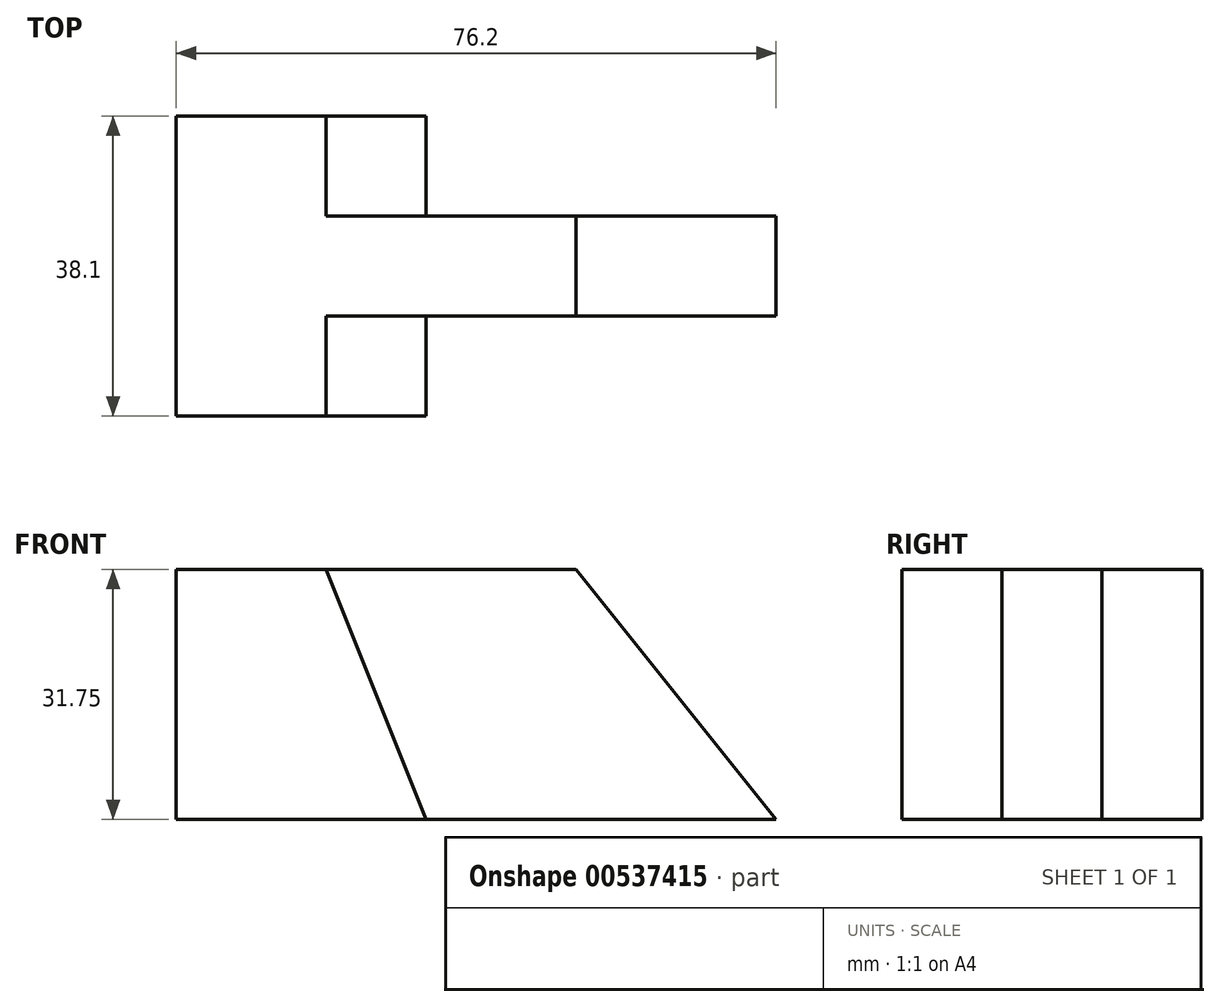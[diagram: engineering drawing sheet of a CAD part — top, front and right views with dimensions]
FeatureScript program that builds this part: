
annotation { "Feature Type Name" : "Feature", "Feature Type Description" : "" }
export const myFeature = defineFeature(function(context is Context, id is Id, definition is map)
    precondition{}
    {
        {
            var Q0;
            Q0=qCreatedBy(makeId("Front.planeOp"),FACE);
            var sketch = newSketch(context, id + "F0", { "sketchPlane" : qUnion([Q0])});
            skLineSegment(sketch, "E0", {"start": v(0, 31.75) * mm, "end": v(0, 0) * mm});
            skLineSegment(sketch, "E1", {"start": v(0, 0) * mm, "end": v(76.2, 0) * mm});
            skLineSegment(sketch, "E2", {"start": v(76.2, 0) * mm, "end": v(76.2, 31.75) * mm});
            skLineSegment(sketch, "E3", {"start": v(76.2, 31.75) * mm, "end": v(0, 31.75) * mm});
            skSolve(sketch);
        }
        {
            var Q0;
            Q0=makeQuery(id+"F0.imprint","IMPRINT",FACE,{"disambiguationData":[TD([[makeQuery(id+"F0.imprint","IMPRINT",EDGE,{"derivedFrom":sQuery(id+"F0.wireOp",EDGE,"E0")}),1.0]])]});
            extrude(context, id + "F1", {"entities" : qUnion([Q0]), "depth" : 38.1 * mm, "offsetDistance" : 25.4 * mm});
        }
        {
            var Q0;
            Q0=makeQuery(id+"F1.opExtrude","SWEPT_FACE",FACE,{"disambiguationData":[OSD([sQuery(id+"F0.wireOp",EDGE,"E2")])]});
            var sketch = newSketch(context, id + "F2", { "sketchPlane" : qUnion([Q0])});
            skSolve(sketch);
        }
        {
            var Q0;
            Q0=makeQuery(id+"F1.opExtrude","CAP_FACE",FACE,{"disambiguationData":[OSD([sQuery(id+"F0.wireOp",EDGE,"E0"),sQuery(id+"F0.wireOp",EDGE,"E1"),sQuery(id+"F0.wireOp",EDGE,"E2"),sQuery(id+"F0.wireOp",EDGE,"E3")])],"isStart":false});
            var sketch = newSketch(context, id + "F3", { "sketchPlane" : qUnion([Q0])});
            skLineSegment(sketch, "E4", {"start": v(19.05, 31.75) * mm, "end": v(31.75, 0) * mm});
            skSolve(sketch);
        }
        {
            var Q0;
            {var subQ0=sQuery(id+"F3.wireOp",EDGE,"E4");Q0=makeQuery(id+"F3.imprint","IMPRINT",FACE,{"disambiguationData":[TD([[makeQuery(id+"F3.imprint","IMPRINT",EDGE,{"derivedFrom":subQ0}),1.0]])]});}
            extrude(context, id + "F4", {"entities" : qUnion([Q0]), "operationType" : NewBodyOperationType.REMOVE, "oppositeDirection" : true, "depth" : 12.7 * mm, "offsetDistance" : 25.4 * mm});
        }
        {
            var Q0;
            Q0=makeQuery(id+"F1.opExtrude","CAP_FACE",FACE,{"disambiguationData":[OSD([sQuery(id+"F0.wireOp",EDGE,"E0"),sQuery(id+"F0.wireOp",EDGE,"E1"),sQuery(id+"F0.wireOp",EDGE,"E2"),sQuery(id+"F0.wireOp",EDGE,"E3")])],"isStart":true});
            var sketch = newSketch(context, id + "F5", { "sketchPlane" : qUnion([Q0])});
            skLineSegment(sketch, "E5", {"start": v(-19.05, 31.75) * mm, "end": v(-31.75, 0) * mm});
            skSolve(sketch);
        }
        {
            var Q0;
            {var subQ0=sQuery(id+"F5.wireOp",EDGE,"E5");Q0=makeQuery(id+"F5.imprint","IMPRINT",FACE,{"disambiguationData":[TD([[makeQuery(id+"F5.imprint","IMPRINT",EDGE,{"derivedFrom":subQ0}),-1.0]])]});}
            extrude(context, id + "F6", {"entities" : qUnion([Q0]), "operationType" : NewBodyOperationType.REMOVE, "oppositeDirection" : true, "depth" : 12.7 * mm, "offsetDistance" : 25.4 * mm});
        }
        {
            var Q0;
            Q0=makeQuery(id+"F4.boolean.opBoolean","COPY",FACE,{"derivedFrom":makeQuery(id+"F4.opExtrude","CAP_FACE",FACE,{"disambiguationData":[OSD([sQuery(id+"F0.wireOp",EDGE,"E1"),sQuery(id+"F0.wireOp",EDGE,"E2"),sQuery(id+"F0.wireOp",EDGE,"E3"),sQuery(id+"F3.wireOp",EDGE,"E4")])],"isStart":false})});
            var sketch = newSketch(context, id + "F7", { "sketchPlane" : qUnion([Q0])});
            skLineSegment(sketch, "E6", {"start": v(50.8, 31.75) * mm, "end": v(76.2, 0) * mm});
            skSolve(sketch);
        }
        {
            var Q0;
            {var subQ0=sQuery(id+"F7.wireOp",EDGE,"E6");Q0=makeQuery(id+"F7.imprint","IMPRINT",FACE,{"disambiguationData":[TD([[makeQuery(id+"F7.imprint","IMPRINT",EDGE,{"derivedFrom":subQ0}),1.0]])]});}
            extrude(context, id + "F8", {"entities" : qUnion([Q0]), "operationType" : NewBodyOperationType.REMOVE, "oppositeDirection" : true, "depth" : 25.4 * mm, "offsetDistance" : 25.4 * mm});
        }
    });
